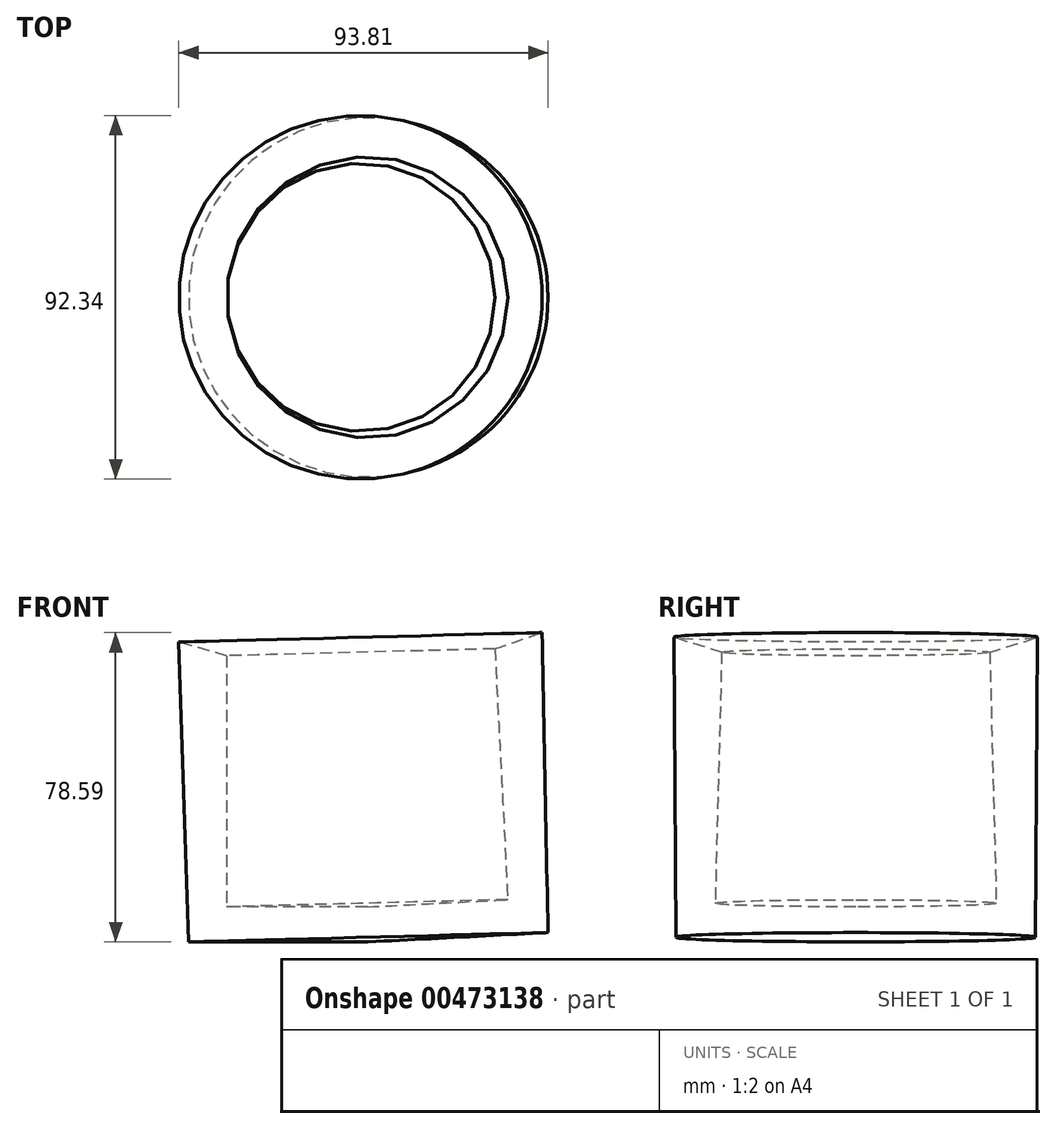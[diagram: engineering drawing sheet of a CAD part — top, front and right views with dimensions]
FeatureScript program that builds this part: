
annotation { "Feature Type Name" : "Feature", "Feature Type Description" : "" }
export const myFeature = defineFeature(function(context is Context, id is Id, definition is map)
    precondition{}
    {
        {
            var Q0;
            Q0=qCreatedBy(makeId("Front.planeOp"),FACE);
            var sketch = newSketch(context, id + "F0", { "sketchPlane" : qUnion([Q0])});
            skLineSegment(sketch, "E0", {"start": v(-47.92, 50.98) * mm, "end": v(-35.72, 47.48) * mm});
            skLineSegment(sketch, "E1", {"start": v(-35.72, 47.48) * mm, "end": v(-35.72, -16.33) * mm});
            skLineSegment(sketch, "E2", {"start": v(-35.72, -16.33) * mm, "end": v(0, -16.33) * mm});
            skLineSegment(sketch, "E3", {"start": v(0, -16.33) * mm, "end": v(0.23, -25.22) * mm});
            skLineSegment(sketch, "E4", {"start": v(0.23, -25.22) * mm, "end": v(-45.5, -25.22) * mm});
            skLineSegment(sketch, "E5", {"start": v(-45.5, -25.22) * mm, "end": v(-47.92, 50.98) * mm});
            skSolve(sketch);
        }
        {
            var Q0;
            Q0=makeQuery(id+"F0.imprint","IMPRINT",FACE,{"disambiguationData":[TD([[makeQuery(id+"F0.imprint","IMPRINT",EDGE,{"derivedFrom":sQuery(id+"F0.wireOp",EDGE,"E0")}),-1.0]])]});
            var Q1;
            Q1=sQuery(id+"F0.wireOp",EDGE,"E3");
            revolve(context, id + "F1", {"entities" : qUnion([Q0]), "axis" : qUnion([Q1]), "revolveType" : RevolveType.FULL});
        }
    });
